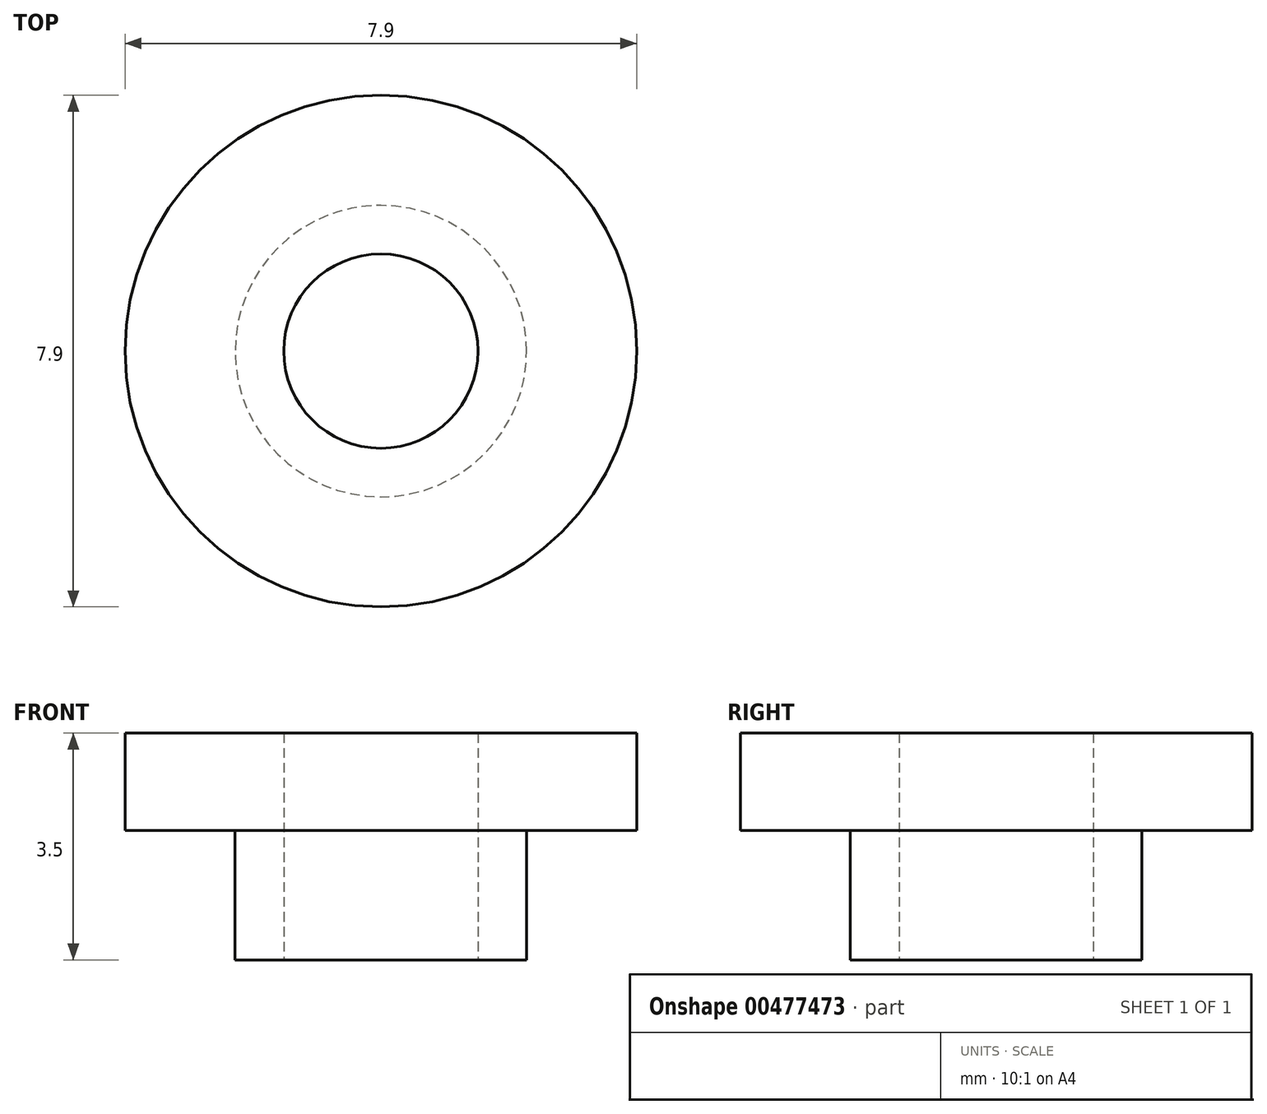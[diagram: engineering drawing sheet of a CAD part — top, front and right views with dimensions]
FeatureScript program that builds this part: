
annotation { "Feature Type Name" : "Feature", "Feature Type Description" : "" }
export const myFeature = defineFeature(function(context is Context, id is Id, definition is map)
    precondition{}
    {
        {
            var Q0;
            Q0=qCreatedBy(makeId("Front.planeOp"),FACE);
            var sketch = newSketch(context, id + "F0", { "sketchPlane" : qUnion([Q0])});
            skLineSegment(sketch, "E0", {"start": v(0, 0) * mm, "end": v(0, 3.5) * mm, "construction": true});
            skLineSegment(sketch, "E1", {"start": v(-1.5, 0) * mm, "end": v(-2.25, 0) * mm});
            skLineSegment(sketch, "E2", {"start": v(-2.25, 0) * mm, "end": v(-2.25, 2) * mm});
            skLineSegment(sketch, "E3", {"start": v(-2.25, 2) * mm, "end": v(-3.95, 2) * mm});
            skLineSegment(sketch, "E4", {"start": v(-3.95, 2) * mm, "end": v(-3.95, 3.5) * mm});
            skLineSegment(sketch, "E5", {"start": v(-3.95, 3.5) * mm, "end": v(-1.5, 3.5) * mm});
            skLineSegment(sketch, "E6", {"start": v(-1.5, 3.5) * mm, "end": v(-1.5, 0) * mm});
            skLineSegment(sketch, "E7.MirrorCS", {"start": v(2.25, 2) * mm, "end": v(3.95, 2) * mm, "construction": true});
            skLineSegment(sketch, "E8.MirrorCS", {"start": v(3.95, 2) * mm, "end": v(3.95, 3.5) * mm, "construction": true});
            skLineSegment(sketch, "E9.MirrorCS", {"start": v(3.95, 3.5) * mm, "end": v(1.5, 3.5) * mm, "construction": true});
            skLineSegment(sketch, "E10.MirrorCS", {"start": v(1.5, 3.5) * mm, "end": v(1.5, 0) * mm, "construction": true});
            skLineSegment(sketch, "E11.MirrorCS", {"start": v(1.5, 0) * mm, "end": v(2.25, 0) * mm, "construction": true});
            skLineSegment(sketch, "E12.MirrorCS", {"start": v(2.25, 0) * mm, "end": v(2.25, 2) * mm, "construction": true});
            skSolve(sketch);
        }
        {
            var Q0;
            Q0 = qSketchRegion(id + "F0", true);
            var Q1;
            Q1=sQuery(id+"F0.wireOp",EDGE,"E0");
            revolve(context, id + "F1", {"entities" : qUnion([Q0]), "axis" : qUnion([Q1]), "revolveType" : RevolveType.FULL});
        }
    });
